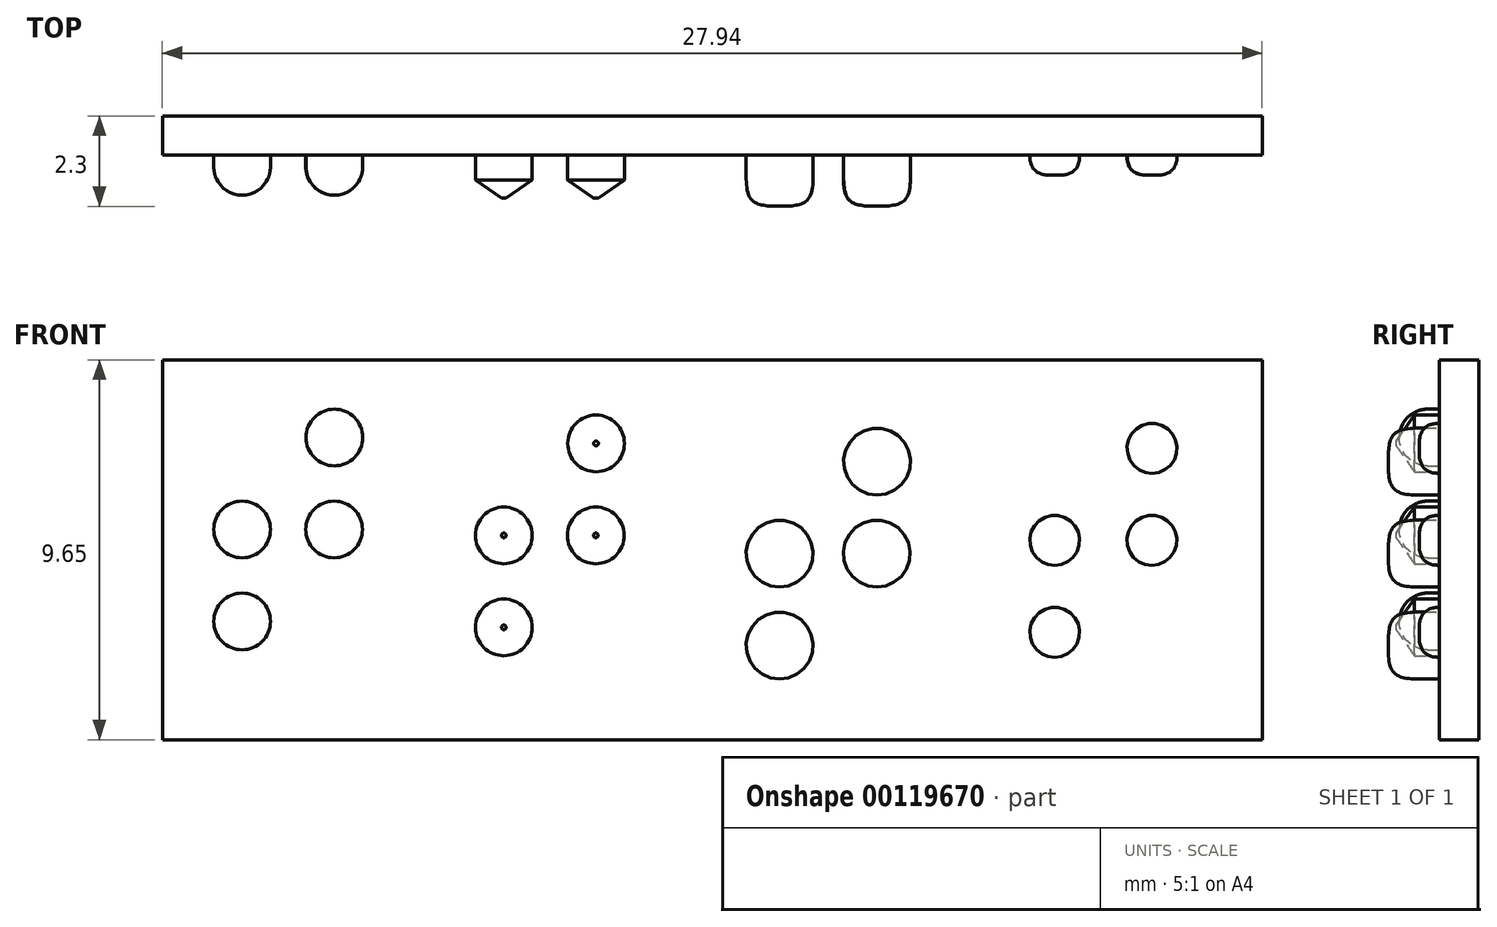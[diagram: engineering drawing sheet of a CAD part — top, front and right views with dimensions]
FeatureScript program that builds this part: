
annotation { "Feature Type Name" : "Feature", "Feature Type Description" : "" }
export const myFeature = defineFeature(function(context is Context, id is Id, definition is map)
    precondition{}
    {
        {
            var Q0;
            Q0=qCreatedBy(makeId("Front.planeOp"),FACE);
            var sketch = newSketch(context, id + "F0", { "sketchPlane" : qUnion([Q0])});
            skCircle(sketch, "E0", {"center": v(-17.35, 47.79) * mm, "radius": 0.72 * mm});
            skLineSegment(sketch, "E1.top", {"start": v(-31.85, 25.4) * mm, "end": v(44.35, 25.4) * mm});
            skCircle(sketch, "E2", {"center": v(-19.7, 43.11) * mm, "radius": 0.72 * mm});
            skCircle(sketch, "E3", {"center": v(-17.36, 45.45) * mm, "radius": 0.72 * mm});
            skCircle(sketch, "E4", {"center": v(-19.7, 45.45) * mm, "radius": 0.72 * mm});
            skCircle(sketch, "E5", {"center": v(-10.7, 47.64) * mm, "radius": 0.72 * mm});
            skCircle(sketch, "E6", {"center": v(-13.05, 42.96) * mm, "radius": 0.72 * mm});
            skCircle(sketch, "E7", {"center": v(-10.7, 45.3) * mm, "radius": 0.72 * mm});
            skCircle(sketch, "E8", {"center": v(-13.05, 45.3) * mm, "radius": 0.72 * mm});
            skCircle(sketch, "E9", {"center": v(-3.56, 47.17) * mm, "radius": 0.85 * mm});
            skCircle(sketch, "E10", {"center": v(-6.04, 42.5) * mm, "radius": 0.85 * mm});
            skCircle(sketch, "E11", {"center": v(-3.57, 44.84) * mm, "radius": 0.85 * mm});
            skCircle(sketch, "E12", {"center": v(-6.04, 44.84) * mm, "radius": 0.85 * mm});
            skCircle(sketch, "E13", {"center": v(3.43, 47.51) * mm, "radius": 0.64 * mm});
            skCircle(sketch, "E14", {"center": v(0.95, 42.84) * mm, "radius": 0.64 * mm});
            skCircle(sketch, "E15", {"center": v(3.42, 45.17) * mm, "radius": 0.64 * mm});
            skCircle(sketch, "E16", {"center": v(0.95, 45.17) * mm, "radius": 0.64 * mm});
            skSolve(sketch);
        }
        {
            var Q0;
            Q0=makeQuery(id+"F0.imprint","IMPRINT",FACE,{"disambiguationData":[TD([[makeQuery(id+"F0.imprint","IMPRINT",EDGE,{"derivedFrom":sQuery(id+"F0.wireOp",EDGE,"E4")}),1.0]])]});
            var Q1;
            Q1=makeQuery(id+"F0.imprint","IMPRINT",FACE,{"disambiguationData":[TD([[makeQuery(id+"F0.imprint","IMPRINT",EDGE,{"derivedFrom":sQuery(id+"F0.wireOp",EDGE,"E3")}),1.0]])]});
            var Q2;
            Q2=makeQuery(id+"F0.imprint","IMPRINT",FACE,{"disambiguationData":[TD([[makeQuery(id+"F0.imprint","IMPRINT",EDGE,{"derivedFrom":sQuery(id+"F0.wireOp",EDGE,"E0")}),1.0]])]});
            var Q3;
            Q3=makeQuery(id+"F0.imprint","IMPRINT",FACE,{"disambiguationData":[TD([[makeQuery(id+"F0.imprint","IMPRINT",EDGE,{"derivedFrom":sQuery(id+"F0.wireOp",EDGE,"E2")}),1.0]])]});
            extrude(context, id + "F1", {"entities" : qUnion([Q0, Q1, Q2, Q3]), "depth" : 1.02 * mm});
        }
        {
            var Q0;
            Q0=makeQuery(id+"F1.opExtrude","CAP_EDGE",EDGE,{"disambiguationData":[OSD([sQuery(id+"F0.wireOp",EDGE,"E4")])],"isStart":false});
            var Q1;
            Q1=makeQuery(id+"F1.opExtrude","CAP_EDGE",EDGE,{"disambiguationData":[OSD([sQuery(id+"F0.wireOp",EDGE,"E2")])],"isStart":false});
            var Q2;
            Q2=makeQuery(id+"F1.opExtrude","CAP_EDGE",EDGE,{"disambiguationData":[OSD([sQuery(id+"F0.wireOp",EDGE,"E3")])],"isStart":false});
            var Q3;
            Q3=makeQuery(id+"F1.opExtrude","CAP_EDGE",EDGE,{"disambiguationData":[OSD([sQuery(id+"F0.wireOp",EDGE,"E0")])],"isStart":false});
            fillet(context, id + "F2", {"entities" : qUnion([Q0, Q1, Q2, Q3]), "radius" : 0.72 * mm, "tangentPropagation" : true, "allowEdgeOverflow" : false});
        }
        {
            var Q0;
            Q0=makeQuery(id+"F0.imprint","IMPRINT",FACE,{"disambiguationData":[TD([[makeQuery(id+"F0.imprint","IMPRINT",EDGE,{"derivedFrom":sQuery(id+"F0.wireOp",EDGE,"E5")}),1.0]])]});
            var Q1;
            Q1=makeQuery(id+"F0.imprint","IMPRINT",FACE,{"disambiguationData":[TD([[makeQuery(id+"F0.imprint","IMPRINT",EDGE,{"derivedFrom":sQuery(id+"F0.wireOp",EDGE,"E7")}),1.0]])]});
            var Q2;
            Q2=makeQuery(id+"F0.imprint","IMPRINT",FACE,{"disambiguationData":[TD([[makeQuery(id+"F0.imprint","IMPRINT",EDGE,{"derivedFrom":sQuery(id+"F0.wireOp",EDGE,"E8")}),1.0]])]});
            var Q3;
            Q3=makeQuery(id+"F0.imprint","IMPRINT",FACE,{"disambiguationData":[TD([[makeQuery(id+"F0.imprint","IMPRINT",EDGE,{"derivedFrom":sQuery(id+"F0.wireOp",EDGE,"E6")}),1.0]])]});
            extrude(context, id + "F3", {"entities" : qUnion([Q0, Q1, Q2, Q3]), "depth" : 1.1 * mm});
        }
        {
            var Q0;
            Q0=makeQuery(id+"F3.opExtrude","CAP_FACE",FACE,{"disambiguationData":[OSD([sQuery(id+"F0.wireOp",EDGE,"E8")])],"isStart":false});
            var Q1;
            Q1=makeQuery(id+"F3.opExtrude","CAP_EDGE",EDGE,{"disambiguationData":[OSD([sQuery(id+"F0.wireOp",EDGE,"E7")])],"isStart":false});
            var Q2;
            Q2=makeQuery(id+"F3.opExtrude","CAP_EDGE",EDGE,{"disambiguationData":[OSD([sQuery(id+"F0.wireOp",EDGE,"E6")])],"isStart":false});
            var Q3;
            Q3=makeQuery(id+"F3.opExtrude","CAP_EDGE",EDGE,{"disambiguationData":[OSD([sQuery(id+"F0.wireOp",EDGE,"E5")])],"isStart":false});
            chamfer(context, id + "F4", {"entities" : qUnion([Q0, Q1, Q2, Q3]), "chamferType" : ChamferType.OFFSET_ANGLE, "width" : 0.66 * mm, "oppositeDirection" : false, "angle" : 35 * degree});
        }
        {
            var Q0;
            Q0=makeQuery(id+"F0.imprint","IMPRINT",FACE,{"disambiguationData":[TD([[makeQuery(id+"F0.imprint","IMPRINT",EDGE,{"derivedFrom":sQuery(id+"F0.wireOp",EDGE,"E14")}),1.0]])]});
            var Q1;
            Q1=makeQuery(id+"F0.imprint","IMPRINT",FACE,{"disambiguationData":[TD([[makeQuery(id+"F0.imprint","IMPRINT",EDGE,{"derivedFrom":sQuery(id+"F0.wireOp",EDGE,"E16")}),1.0]])]});
            var Q2;
            Q2=makeQuery(id+"F0.imprint","IMPRINT",FACE,{"disambiguationData":[TD([[makeQuery(id+"F0.imprint","IMPRINT",EDGE,{"derivedFrom":sQuery(id+"F0.wireOp",EDGE,"E15")}),1.0]])]});
            var Q3;
            Q3=makeQuery(id+"F0.imprint","IMPRINT",FACE,{"disambiguationData":[TD([[makeQuery(id+"F0.imprint","IMPRINT",EDGE,{"derivedFrom":sQuery(id+"F0.wireOp",EDGE,"E13")}),1.0]])]});
            var Q4;
            Q4=sQuery(id+"F0.wireOp",EDGE,"E12");
            extrude(context, id + "F5", {"entities" : qUnion([Q0, Q1, Q2, Q3]), "surfaceEntities" : qUnion([Q4]), "depth" : 0.5 * mm});
        }
        {
            var Q0;
            Q0=makeQuery(id+"F0.imprint","IMPRINT",FACE,{"disambiguationData":[TD([[makeQuery(id+"F0.imprint","IMPRINT",EDGE,{"derivedFrom":sQuery(id+"F0.wireOp",EDGE,"E9")}),1.0]])]});
            var Q1;
            Q1=makeQuery(id+"F0.imprint","IMPRINT",FACE,{"disambiguationData":[TD([[makeQuery(id+"F0.imprint","IMPRINT",EDGE,{"derivedFrom":sQuery(id+"F0.wireOp",EDGE,"E12")}),1.0]])]});
            var Q2;
            Q2=makeQuery(id+"F0.imprint","IMPRINT",FACE,{"disambiguationData":[TD([[makeQuery(id+"F0.imprint","IMPRINT",EDGE,{"derivedFrom":sQuery(id+"F0.wireOp",EDGE,"E10")}),1.0]])]});
            var Q3;
            Q3=makeQuery(id+"F0.imprint","IMPRINT",FACE,{"disambiguationData":[TD([[makeQuery(id+"F0.imprint","IMPRINT",EDGE,{"derivedFrom":sQuery(id+"F0.wireOp",EDGE,"E11")}),1.0]])]});
            var Q4;
            Q4=sQuery(id+"F0.wireOp",EDGE,"E12");
            var Q5;
            Q5=sQuery(id+"F0.wireOp",EDGE,"E11");
            var Q6;
            Q6=sQuery(id+"F0.wireOp",EDGE,"E9");
            var Q7;
            Q7=sQuery(id+"F0.wireOp",EDGE,"E10");
            extrude(context, id + "F6", {"entities" : qUnion([Q0, Q1, Q2, Q3]), "surfaceEntities" : qUnion([Q4, Q5, Q6, Q7]), "depth" : 1.3 * mm});
        }
        {
            var Q0;
            Q0=makeQuery(id+"F6.opExtrude","CAP_FACE",FACE,{"disambiguationData":[OSD([sQuery(id+"F0.wireOp",EDGE,"E9")])],"isStart":false});
            var Q1;
            Q1=makeQuery(id+"F6.opExtrude","CAP_EDGE",EDGE,{"disambiguationData":[OSD([sQuery(id+"F0.wireOp",EDGE,"E11")])],"isStart":false});
            var Q2;
            Q2=makeQuery(id+"F6.opExtrude","CAP_FACE",FACE,{"disambiguationData":[OSD([sQuery(id+"F0.wireOp",EDGE,"E12")])],"isStart":false});
            var Q3;
            Q3=makeQuery(id+"F6.opExtrude","CAP_EDGE",EDGE,{"disambiguationData":[OSD([sQuery(id+"F0.wireOp",EDGE,"E10")])],"isStart":false});
            fillet(context, id + "F7", {"entities" : qUnion([Q0, Q1, Q2, Q3]), "radius" : 0.76 * mm, "rho" : 0.6, "crossSection" : FilletCrossSection.CONIC, "allowEdgeOverflow" : false});
        }
        {
            var Q0;
            Q0=makeQuery(id+"F5.opExtrude","CAP_FACE",FACE,{"disambiguationData":[OSD([sQuery(id+"F0.wireOp",EDGE,"E16")])],"isStart":false});
            var Q1;
            Q1=makeQuery(id+"F5.opExtrude","CAP_FACE",FACE,{"disambiguationData":[OSD([sQuery(id+"F0.wireOp",EDGE,"E15")])],"isStart":false});
            var Q2;
            Q2=makeQuery(id+"F5.opExtrude","CAP_FACE",FACE,{"disambiguationData":[OSD([sQuery(id+"F0.wireOp",EDGE,"E13")])],"isStart":false});
            var Q3;
            Q3=makeQuery(id+"F5.opExtrude","CAP_FACE",FACE,{"disambiguationData":[OSD([sQuery(id+"F0.wireOp",EDGE,"E14")])],"isStart":false});
            fillet(context, id + "F8", {"entities" : qUnion([Q0, Q1, Q2, Q3]), "radius" : 0.5 * mm, "tangentPropagation" : true, "rho" : .5, "crossSection" : FilletCrossSection.CONIC, "allowEdgeOverflow" : false});
        }
        {
            var Q0;
            Q0=qCreatedBy(makeId("Front.planeOp"),FACE);
            var sketch = newSketch(context, id + "F9", { "sketchPlane" : qUnion([Q0])});
            skLineSegment(sketch, "E17.bottom", {"start": v(-21.72, 49.76) * mm, "end": v(6.22, 49.76) * mm});
            skLineSegment(sketch, "E17.top", {"start": v(-21.72, 40.1) * mm, "end": v(6.22, 40.1) * mm});
            skLineSegment(sketch, "E17.left", {"start": v(-21.72, 49.76) * mm, "end": v(-21.72, 40.1) * mm});
            skLineSegment(sketch, "E17.right", {"start": v(6.22, 49.76) * mm, "end": v(6.22, 40.1) * mm});
            skSolve(sketch);
        }
        {
            var Q0;
            Q0 = qSketchRegion(id + "F9", true);
            extrude(context, id + "F10", {"entities" : qUnion([Q0]), "oppositeDirection" : true, "depth" : 1 * mm});
        }
    });
